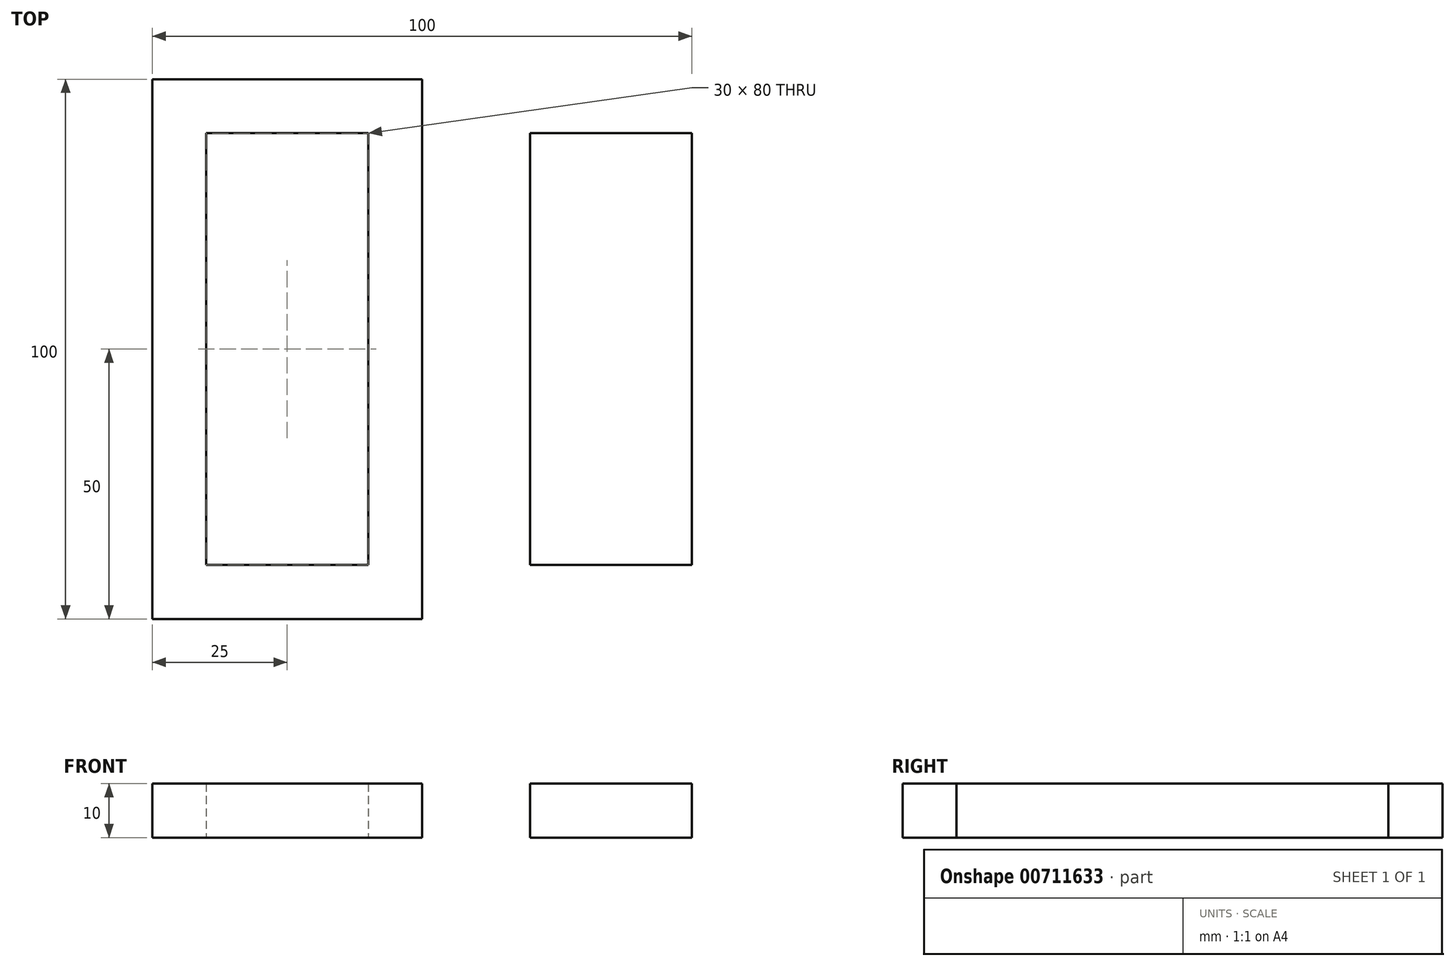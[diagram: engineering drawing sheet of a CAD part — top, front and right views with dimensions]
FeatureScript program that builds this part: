
annotation { "Feature Type Name" : "Feature", "Feature Type Description" : "" }
export const myFeature = defineFeature(function(context is Context, id is Id, definition is map)
    precondition{}
    {
        {
            var Q0;
            Q0=qCreatedBy(makeId("Top.planeOp"),FACE);
            var sketch = newSketch(context, id + "F0", { "sketchPlane" : qUnion([Q0])});
            skLineSegment(sketch, "E0.bottom", {"start": v(-25, 50) * mm, "end": v(25, 50) * mm});
            skLineSegment(sketch, "E0.top", {"start": v(-25, -50) * mm, "end": v(25, -50) * mm});
            skLineSegment(sketch, "E0.left", {"start": v(-25, 50) * mm, "end": v(-25, -50) * mm});
            skLineSegment(sketch, "E0.right", {"start": v(25, 50) * mm, "end": v(25, -50) * mm});
            skLineSegment(sketch, "E1.bottom", {"start": v(-15, 40) * mm, "end": v(15, 40) * mm});
            skLineSegment(sketch, "E1.top", {"start": v(-15, -40) * mm, "end": v(15, -40) * mm});
            skLineSegment(sketch, "E1.left", {"start": v(-15, 40) * mm, "end": v(-15, -40) * mm});
            skLineSegment(sketch, "E1.right", {"start": v(15, 40) * mm, "end": v(15, -40) * mm});
            skLineSegment(sketch, "E2", {"start": v(-25, 50) * mm, "end": v(25, -50) * mm, "construction": true});
            skPoint(sketch, "E3", {"position": v(0, 0) * mm});
            skLineSegment(sketch, "E4", {"start": v(15, 40) * mm, "end": v(-15, -40) * mm, "construction": true});
            skLineSegment(sketch, "E5.bottom", {"start": v(45, 40) * mm, "end": v(75, 40) * mm});
            skLineSegment(sketch, "E5.top", {"start": v(45, -40) * mm, "end": v(75, -40) * mm});
            skLineSegment(sketch, "E5.left", {"start": v(45, 40) * mm, "end": v(45, -40) * mm});
            skLineSegment(sketch, "E5.right", {"start": v(75, 40) * mm, "end": v(75, -40) * mm});
            skLineSegment(sketch, "E6", {"start": v(15, -40) * mm, "end": v(45, -40) * mm, "construction": true});
            skSolve(sketch);
        }
        {
            var Q0;
            Q0 = qSketchRegion(id + "F0", true);
            extrude(context, id + "F1", {"entities" : qUnion([Q0]), "depth" : 10 * mm, "offsetDistance" : 25 * mm});
        }
    });
